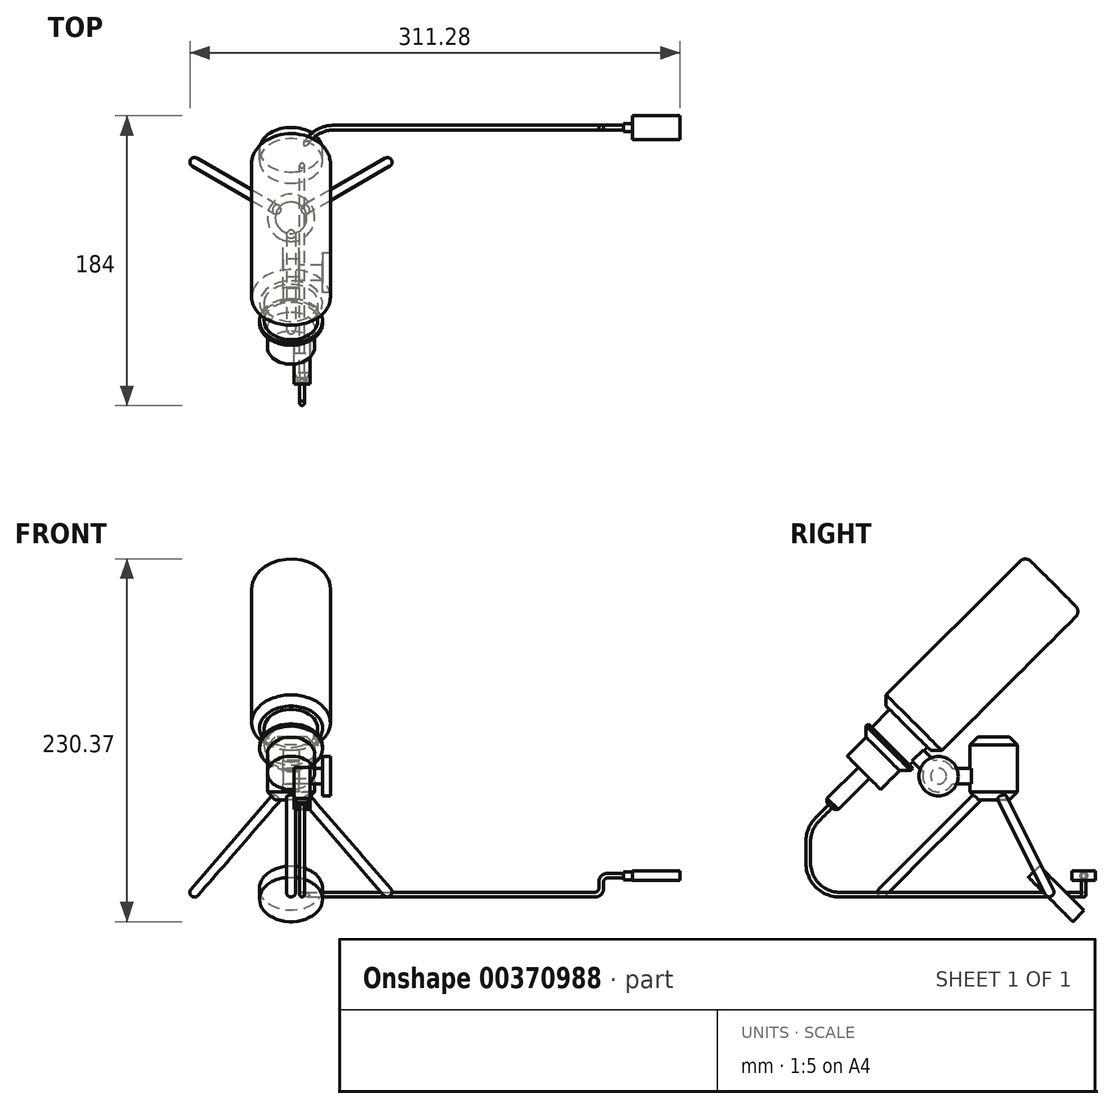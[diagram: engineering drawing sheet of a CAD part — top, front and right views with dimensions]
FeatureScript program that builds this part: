
annotation { "Feature Type Name" : "Feature", "Feature Type Description" : "" }
export const myFeature = defineFeature(function(context is Context, id is Id, definition is map)
    precondition{}
    {
        {
            var Q0;
            Q0=qCreatedBy(makeId("Top.planeOp"),FACE);
            var sketch = newSketch(context, id + "F0", { "sketchPlane" : qUnion([Q0])});
            skCircle(sketch, "E0", {"center": v(0, 0) * mm, "radius": 15 * mm});
            skSolve(sketch);
        }
        {
            var Q0;
            Q0 = qSketchRegion(id + "F0", true);
            extrude(context, id + "F1", {"entities" : qUnion([Q0]), "depth" : 40 * mm});
        }
        {
            var Q0;
            Q0=makeQuery(id+"F1.opExtrude","CAP_EDGE",EDGE,{"disambiguationData":[OSD([sQuery(id+"F0.wireOp",EDGE,"E0")])],"isStart":true});
            var Q1;
            Q1=makeQuery(id+"F1.opExtrude","CAP_EDGE",EDGE,{"disambiguationData":[OSD([sQuery(id+"F0.wireOp",EDGE,"E0")])],"isStart":false});
            chamfer(context, id + "F2", {"entities" : qUnion([Q0, Q1]), "width" : 5 * mm, "tangentPropagation" : true});
        }
        {
            var Q0;
            Q0=qCreatedBy(makeId("Right.planeOp"),FACE);
            var sketch = newSketch(context, id + "F3", { "sketchPlane" : qUnion([Q0])});
            skLineSegment(sketch, "E1", {"start": v(-72.83, -56.59) * mm, "end": v(-2.12, 14.12) * mm});
            skLineSegment(sketch, "E2", {"start": v(-2.12, 14.12) * mm, "end": v(0, 12) * mm});
            skArc(sketch, "E3", {"start": v(-72.83, -56.59) * mm, "mid": v(-73.71, -58.71) * mm, "end": v(-72.83, -60.83) * mm});
            skLineSegment(sketch, "E4", {"start": v(-72.83, -60.83) * mm, "end": v(0, 12) * mm});
            skSolve(sketch);
        }
        {
            var Q0;
            Q0 = qSketchRegion(id + "F3", true);
            var Q1;
            Q1=sQuery(id+"F3.wireOp",EDGE,"E4");
            revolve(context, id + "F4", {"operationType" : NewBodyOperationType.ADD, "entities" : qUnion([Q0]), "axis" : qUnion([Q1]), "revolveType" : RevolveType.FULL});
        }
        {
            var Q0;
            Q0=qCreatedBy(makeId("Right.planeOp"),FACE);
            var sketch = newSketch(context, id + "F5", { "sketchPlane" : qUnion([Q0])});
            skLineSegment(sketch, "E5", {"start": v(0, 0) * mm, "end": v(0, -28.47) * mm});
            skSolve(sketch);
        }
        {
            var Q0;
            Q0=qCreatedBy(makeId("Right.planeOp"),FACE);
            var Q1;
            Q1=sQuery(id+"F5.wireOp",EDGE,"E5");
            cPlane(context, id + "F6", {"entities" : qUnion([Q0, Q1]), "cplaneType" : CPlaneType.LINE_ANGLE, "offset" : 25 * mm, "angle" : 120 * degree, "oppositeDirection" : true, "width" : 150 * mm, "height" : 150 * mm});
        }
        {
            var Q0;
            Q0=qCreatedBy(id+"F6.planeOp",FACE);
            var sketch = newSketch(context, id + "F7", { "sketchPlane" : qUnion([Q0])});
            skLineSegment(sketch, "E6", {"start": v(0, 12) * mm, "end": v(72.73, -60.73) * mm});
            skLineSegment(sketch, "E7", {"start": v(72.73, -56.5) * mm, "end": v(2.02, 14.22) * mm});
            skLineSegment(sketch, "E8", {"start": v(2.02, 14.22) * mm, "end": v(0, 12) * mm});
            skArc(sketch, "E9", {"start": v(72.73, -56.5) * mm, "mid": v(73.61, -58.61) * mm, "end": v(72.73, -60.73) * mm});
            skPoint(sketch, "E10.orphan", {"position": v(70.61, -61.61) * mm});
            skSolve(sketch);
        }
        {
            var Q0;
            Q0 = qSketchRegion(id + "F7", true);
            var Q1;
            Q1=sQuery(id+"F7.wireOp",EDGE,"E6");
            revolve(context, id + "F8", {"operationType" : NewBodyOperationType.ADD, "entities" : qUnion([Q0]), "axis" : qUnion([Q1]), "revolveType" : RevolveType.FULL});
        }
        {
            var Q0;
            Q0=qCreatedBy(id+"F6.planeOp",FACE);
            var Q1;
            Q1=sQuery(id+"F5.wireOp",EDGE,"E5");
            cPlane(context, id + "F9", {"entities" : qUnion([Q0, Q1]), "cplaneType" : CPlaneType.LINE_ANGLE, "offset" : 25 * mm, "angle" : 120 * degree, "oppositeDirection" : true, "width" : 150 * mm, "height" : 150 * mm});
        }
        {
            var Q0;
            Q0=qCreatedBy(id+"F9.planeOp",FACE);
            var sketch = newSketch(context, id + "F10", { "sketchPlane" : qUnion([Q0])});
            skLineSegment(sketch, "E11", {"start": v(0, 12) * mm, "end": v(-72.89, -60.89) * mm});
            skLineSegment(sketch, "E12", {"start": v(-72.89, -56.64) * mm, "end": v(-2.18, 14.07) * mm});
            skLineSegment(sketch, "E13", {"start": v(-2.18, 14.07) * mm, "end": v(0, 12) * mm});
            skArc(sketch, "E14", {"start": v(-72.89, -56.64) * mm, "mid": v(-73.77, -58.77) * mm, "end": v(-72.89, -60.89) * mm});
            skPoint(sketch, "E15.orphan", {"position": v(-70.77, -61.77) * mm});
            skSolve(sketch);
        }
        {
            var Q0;
            Q0 = qSketchRegion(id + "F10", true);
            var Q1;
            Q1=sQuery(id+"F10.wireOp",EDGE,"E11");
            revolve(context, id + "F11", {"operationType" : NewBodyOperationType.ADD, "entities" : qUnion([Q0]), "axis" : qUnion([Q1]), "revolveType" : RevolveType.FULL});
        }
        {
            var Q0;
            Q0=qCreatedBy(makeId("Front.planeOp"),FACE);
            var sketch = newSketch(context, id + "F12", { "sketchPlane" : qUnion([Q0])});
            skLineSegment(sketch, "E16.bottom", {"start": v(-5, 20) * mm, "end": v(5, 20) * mm});
            skLineSegment(sketch, "E16.top", {"start": v(-5, 10) * mm, "end": v(5, 10) * mm});
            skLineSegment(sketch, "E16.left", {"start": v(-5, 20) * mm, "end": v(-5, 10) * mm});
            skLineSegment(sketch, "E16.right", {"start": v(5, 20) * mm, "end": v(5, 10) * mm});
            skSolve(sketch);
        }
        {
            var Q0;
            Q0 = qSketchRegion(id + "F12", true);
            extrude(context, id + "F13", {"entities" : qUnion([Q0]), "operationType" : NewBodyOperationType.ADD, "depth" : 30 * mm});
        }
        {
            var Q0;
            Q0=qCreatedBy(makeId("Right.planeOp"),FACE);
            var sketch = newSketch(context, id + "F14", { "sketchPlane" : qUnion([Q0])});
            skCircle(sketch, "E17", {"center": v(-35, 15) * mm, "radius": 10 * mm});
            skLineSegment(sketch, "E18", {"start": v(-38.54, 11.46) * mm, "end": v(-35, 15) * mm});
            skLineSegment(sketch, "E19", {"start": v(-38.54, 11.46) * mm, "end": v(-52.68, 25.6) * mm});
            skLineSegment(sketch, "E20", {"start": v(-52.68, 25.6) * mm, "end": v(-45.6, 32.68) * mm});
            skLineSegment(sketch, "E21", {"start": v(-45.6, 32.68) * mm, "end": v(-31.46, 18.54) * mm});
            skLineSegment(sketch, "E22", {"start": v(-31.46, 18.54) * mm, "end": v(-35, 15) * mm});
            skSolve(sketch);
        }
        {
            var Q0;
            Q0 = qSketchRegion(id + "F14", true);
            extrude(context, id + "F15", {"entities" : qUnion([Q0]), "operationType" : NewBodyOperationType.ADD, "endBound" : BoundingType.SYMMETRIC, "depth" : 10 * mm});
        }
        {
            var Q0;
            Q0=makeQuery(id+"F15.opExtrude","SWEPT_FACE",FACE,{"disambiguationData":[OSD([sQuery(id+"F14.wireOp",EDGE,"E21")])]});
            var sketch = newSketch(context, id + "F16", { "sketchPlane" : qUnion([Q0])});
            skPoint(sketch, "E23.first.point", {"position": v(0, -67.78) * mm});
            skPoint(sketch, "E23.first.point.positionSnap0", {"position": v(0, -55.36) * mm});
            skPoint(sketch, "E23.second.point", {"position": v(0, -49.63) * mm});
            skPoint(sketch, "E23.second.point.positionSnap0", {"position": v(0, -55.36) * mm});
            skPoint(sketch, "E23.third.point", {"position": v(-9.57, -55.36) * mm});
            skPoint(sketch, "E23.third.point.positionSnap0", {"position": v(0, -55.36) * mm});
            skCircle(sketch, "E24", {"center": v(0, -70.36) * mm, "radius": 20 * mm});
            skSolve(sketch);
        }
        {
            var Q0;
            Q0 = qSketchRegion(id + "F16", true);
            extrude(context, id + "F17", {"entities" : qUnion([Q0]), "operationType" : NewBodyOperationType.ADD, "oppositeDirection" : true, "depth" : 10 * mm});
        }
        {
            var Q0;
            Q0=qCreatedBy(makeId("Right.planeOp"),FACE);
            var sketch = newSketch(context, id + "F18", { "sketchPlane" : qUnion([Q0])});
            skLineSegment(sketch, "E25", {"start": v(-82.38, 17.12) * mm, "end": v(37.83, 137.33) * mm});
            skLineSegment(sketch, "E26", {"start": v(37.83, 137.33) * mm, "end": v(20.15, 155) * mm});
            skLineSegment(sketch, "E27", {"start": v(20.15, 155) * mm, "end": v(-71.77, 63.08) * mm});
            skLineSegment(sketch, "E28", {"start": v(-71.77, 63.08) * mm, "end": v(-66.11, 57.43) * mm});
            skLineSegment(sketch, "E29", {"start": v(-66.11, 57.43) * mm, "end": v(-77.43, 46.11) * mm});
            skLineSegment(sketch, "E30", {"start": v(-84.5, 43.28) * mm, "end": v(-80.96, 39.75) * mm});
            skLineSegment(sketch, "E31", {"start": v(-89.45, 24.2) * mm, "end": v(-82.38, 17.12) * mm});
            skPoint(sketch, "E32.end.orphan", {"position": v(-71.77, 45.43) * mm});
            skLineSegment(sketch, "E33", {"start": v(-77.43, 46.11) * mm, "end": v(-79.55, 48.23) * mm});
            skLineSegment(sketch, "E34", {"start": v(-79.55, 48.23) * mm, "end": v(-84.5, 43.28) * mm});
            skLineSegment(sketch, "E35", {"start": v(-80.96, 39.75) * mm, "end": v(-92.98, 27.73) * mm});
            skLineSegment(sketch, "E36", {"start": v(-92.98, 27.73) * mm, "end": v(-89.45, 24.2) * mm});
            skPoint(sketch, "E37.start.orphan", {"position": v(-77.43, 36.21) * mm});
            skSolve(sketch);
        }
        {
            var Q0;
            Q0 = qSketchRegion(id + "F18", true);
            var Q1;
            Q1=sQuery(id+"F18.wireOp",EDGE,"E25");
            revolve(context, id + "F19", {"operationType" : NewBodyOperationType.ADD, "entities" : qUnion([Q0]), "axis" : qUnion([Q1]), "revolveType" : RevolveType.FULL});
        }
        {
            var Q0;
            Q0=makeQuery(id+"F19.opRevolve","SWEPT_EDGE",EDGE,{"disambiguationData":[OSD([sQuery(id+"F18.wireOp",EDGE,"E26"),sQuery(id+"F18.wireOp",EDGE,"E27")])]});
            fillet(context, id + "F20", {"entities" : qUnion([Q0]), "radius" : 5 * mm, "tangentPropagation" : true, "allowEdgeOverflow" : false});
        }
        {
            var Q0;
            Q0=makeQuery(id+"F19.opRevolve","SWEPT_EDGE",EDGE,{"disambiguationData":[OSD([sQuery(id+"F18.wireOp",EDGE,"E27"),sQuery(id+"F18.wireOp",EDGE,"E28")])]});
            var Q1;
            Q1=makeQuery(id+"F19.opRevolve","SWEPT_EDGE",EDGE,{"disambiguationData":[OSD([sQuery(id+"F18.wireOp",EDGE,"E30"),sQuery(id+"F18.wireOp",EDGE,"E34")])]});
            chamfer(context, id + "F21", {"entities" : qUnion([Q0, Q1]), "width" : 5 * mm, "tangentPropagation" : true});
        }
        {
            var Q0;
            Q0=makeQuery(id+"F15.boolean.opBoolean","MERGE",FACE,{"derivedFrom":[makeQuery(id+"F13.opExtrude","SWEPT_FACE",FACE,{"disambiguationData":[OSD([sQuery(id+"F12.wireOp",EDGE,"E16.right")])]}),makeQuery(id+"F15.opExtrude","CAP_FACE",FACE,{"disambiguationData":[OSD([sQuery(id+"F14.wireOp",EDGE,"E17"),sQuery(id+"F14.wireOp",EDGE,"E19"),sQuery(id+"F14.wireOp",EDGE,"E20"),sQuery(id+"F14.wireOp",EDGE,"E21")])],"isStart":false})]});
            var sketch = newSketch(context, id + "F22", { "sketchPlane" : qUnion([Q0])});
            skCircle(sketch, "E38", {"center": v(-35, 15) * mm, "radius": 5 * mm});
            skSolve(sketch);
        }
        {
            var Q0;
            Q0 = qSketchRegion(id + "F22", true);
            extrude(context, id + "F23", {"entities" : qUnion([Q0]), "operationType" : NewBodyOperationType.ADD, "depth" : 15 * mm});
        }
        {
            var Q0;
            Q0=makeQuery(id+"F23.opExtrude","CAP_FACE",FACE,{"disambiguationData":[OSD([sQuery(id+"F22.wireOp",EDGE,"E38")])],"isStart":false});
            var sketch = newSketch(context, id + "F24", { "sketchPlane" : qUnion([Q0])});
            skCircle(sketch, "E39", {"center": v(-35, 15) * mm, "radius": 12.5 * mm});
            skSolve(sketch);
        }
        {
            var Q0;
            Q0 = qSketchRegion(id + "F24", true);
            extrude(context, id + "F25", {"entities" : qUnion([Q0]), "operationType" : NewBodyOperationType.ADD, "depth" : 5 * mm});
        }
        {
            var Q0;
            Q0=makeQuery(id+"F19.opRevolve","SWEPT_FACE",FACE,{"disambiguationData":[OSD([sQuery(id+"F18.wireOp",EDGE,"E31")])]});
            var sketch = newSketch(context, id + "F26", { "sketchPlane" : qUnion([Q0])});
            skLineSegment(sketch, "E40.bottom", {"start": v(2, 65.36) * mm, "end": v(12, 65.36) * mm});
            skLineSegment(sketch, "E40.top", {"start": v(2, 75.36) * mm, "end": v(12, 75.36) * mm});
            skLineSegment(sketch, "E40.left", {"start": v(2, 65.36) * mm, "end": v(2, 75.36) * mm});
            skLineSegment(sketch, "E40.right", {"start": v(12, 65.36) * mm, "end": v(12, 75.36) * mm});
            skSolve(sketch);
        }
        {
            var Q0;
            Q0 = qSketchRegion(id + "F26", true);
            extrude(context, id + "F27", {"entities" : qUnion([Q0]), "operationType" : NewBodyOperationType.ADD, "depth" : 30 * mm});
        }
        {
            var Q0;
            Q0=makeQuery(id+"F27.opExtrude","CAP_FACE",FACE,{"disambiguationData":[OSD([sQuery(id+"F26.wireOp",EDGE,"E40.bottom"),sQuery(id+"F26.wireOp",EDGE,"E40.top"),sQuery(id+"F26.wireOp",EDGE,"E40.left"),sQuery(id+"F26.wireOp",EDGE,"E40.right")])],"isStart":false});
            chamfer(context, id + "F28", {"entities" : qUnion([Q0]), "width" : 2 * mm, "tangentPropagation" : true});
        }
        {
            var Q0;
            Q0=qCreatedBy(makeId("Right.planeOp"),FACE);
            var sketch = newSketch(context, id + "F29", { "sketchPlane" : qUnion([Q0])});
            skLineSegment(sketch, "E41", {"start": v(-103.59, -4.1) * mm, "end": v(-111.87, -12.38) * mm});
            skLineSegment(sketch, "E42", {"start": v(-117.73, -26.52) * mm, "end": v(-117.73, -40.23) * mm});
            skLineSegment(sketch, "E43", {"start": v(-97.73, -60.23) * mm, "end": v(32.27, -60.23) * mm});
            skPoint(sketch, "E44.visualSharp", {"position": v(-117.73, -18.23) * mm});
            skArc(sketch, "E44.filletArc", {"start": v(-111.87, -12.38) * mm, "mid": v(-116.2, -18.86) * mm, "end": v(-117.73, -26.52) * mm});
            skPoint(sketch, "E45.visualSharp", {"position": v(-117.73, -60.23) * mm});
            skArc(sketch, "E45.filletArc", {"start": v(-117.73, -40.23) * mm, "mid": v(-111.87, -54.38) * mm, "end": v(-97.73, -60.23) * mm});
            skSolve(sketch);
        }
        {
            var Q0;
            Q0=makeQuery(id+"F27.opExtrude","CAP_FACE",FACE,{"disambiguationData":[OSD([sQuery(id+"F26.wireOp",EDGE,"E40.bottom"),sQuery(id+"F26.wireOp",EDGE,"E40.top"),sQuery(id+"F26.wireOp",EDGE,"E40.left"),sQuery(id+"F26.wireOp",EDGE,"E40.right")])],"isStart":false});
            var sketch = newSketch(context, id + "F30", { "sketchPlane" : qUnion([Q0])});
            skCircle(sketch, "E46", {"center": v(7, 70.36) * mm, "radius": 1.5 * mm});
            skSolve(sketch);
        }
        {
            var Q0;
            Q0 = qSketchRegion(id + "F30", true);
            var Q1;
            Q1 = qConstructionFilter(qBodyType(qCreatedBy(id + "F29" ,EDGE), BodyType.WIRE), ConstructionObject.NO);
            sweep(context, id + "F31", {"operationType" : NewBodyOperationType.ADD, "profiles" : qUnion([Q0]), "path" : qUnion([Q1])});
        }
        {
            var Q0;
            Q0=makeQuery(id+"F31.opSweep","CAP_FACE",FACE,{"disambiguationData":[OSD([sQuery(id+"F29.wireOp",VERTEX,"E43.end"),sQuery(id+"F30.wireOp",EDGE,"E46")])],"isStart":false});
            var sketch = newSketch(context, id + "F32", { "sketchPlane" : qUnion([Q0])});
            skCircle(sketch, "E47", {"center": v(-7, -60.23) * mm, "radius": 1.5 * mm});
            skSolve(sketch);
        }
        {
            var Q0;
            Q0 = qBodyType(qCreatedBy(id + "F32" ,EDGE), BodyType.WIRE);
            cPlane(context, id + "F33", {"entities" : qUnion([Q0]), "cplaneType" : CPlaneType.LINE_ANGLE, "offset" : 25 * mm, "angle" : 0 * degree, "width" : 150 * mm, "height" : 150 * mm});
        }
        {
            var Q0;
            Q0=qCreatedBy(id+"F33.planeOp",FACE);
            var sketch = newSketch(context, id + "F34", { "sketchPlane" : qUnion([Q0])});
            skLineSegment(sketch, "E48", {"start": v(27, 57.27) * mm, "end": v(177, 57.27) * mm});
            skLineSegment(sketch, "E49", {"start": v(7, 32.27) * mm, "end": v(7, 37.27) * mm});
            skArc(sketch, "E50", {"start": v(7, 37.27) * mm, "mid": v(12.86, 51.41) * mm, "end": v(27, 57.27) * mm});
            skSolve(sketch);
        }
        {
            var Q0;
            Q0 = qSketchRegion(id + "F32", true);
            var Q1;
            Q1 = qConstructionFilter(qBodyType(qCreatedBy(id + "F34" ,EDGE), BodyType.WIRE), ConstructionObject.NO);
            sweep(context, id + "F35", {"operationType" : NewBodyOperationType.ADD, "profiles" : qUnion([Q0]), "path" : qUnion([Q1])});
        }
        {
            var Q0;
            Q0=makeQuery(id+"F35.opSweep","CAP_FACE",FACE,{"disambiguationData":[OSD([sQuery(id+"F32.wireOp",EDGE,"E47"),sQuery(id+"F34.wireOp",VERTEX,"E48.end")])],"isStart":false});
            var sketch = newSketch(context, id + "F36", { "sketchPlane" : qUnion([Q0])});
            skCircle(sketch, "E51", {"center": v(57.27, -60.23) * mm, "radius": 1.5 * mm});
            skSolve(sketch);
        }
        {
            var Q0;
            Q0=sQuery(id+"F36.wireOp",EDGE,"E51");
            cPlane(context, id + "F37", {"entities" : qUnion([Q0]), "cplaneType" : CPlaneType.LINE_ANGLE, "offset" : 25 * mm, "angle" : 0 * degree, "width" : 150 * mm, "height" : 150 * mm});
        }
        {
            var Q0;
            Q0=qCreatedBy(id+"F37.planeOp",FACE);
            var sketch = newSketch(context, id + "F38", { "sketchPlane" : qUnion([Q0])});
            skLineSegment(sketch, "E52", {"start": v(-177, -60.23) * mm, "end": v(-193, -60.23) * mm});
            skLineSegment(sketch, "E53", {"start": v(-197, -56.23) * mm, "end": v(-197, -52.23) * mm});
            skLineSegment(sketch, "E54", {"start": v(-201, -48.23) * mm, "end": v(-217, -48.23) * mm});
            skArc(sketch, "E55", {"start": v(-193, -60.23) * mm, "mid": v(-195.83, -59.06) * mm, "end": v(-197, -56.23) * mm});
            skArc(sketch, "E56", {"start": v(-197, -52.23) * mm, "mid": v(-198.17, -49.4) * mm, "end": v(-201, -48.23) * mm});
            skPoint(sketch, "E57.0", {"position": v(-177, -60.23) * mm});
            skSolve(sketch);
        }
        {
            var Q0;
            Q0 = qSketchRegion(id + "F36", true);
            var Q1;
            Q1 = qConstructionFilter(qBodyType(qCreatedBy(id + "F38" ,EDGE), BodyType.WIRE), ConstructionObject.NO);
            sweep(context, id + "F39", {"operationType" : NewBodyOperationType.ADD, "profiles" : qUnion([Q0]), "path" : qUnion([Q1])});
        }
        {
            var Q0;
            Q0=makeQuery(id+"F39.opSweep","CAP_FACE",FACE,{"disambiguationData":[OSD([sQuery(id+"F36.wireOp",EDGE,"E51"),sQuery(id+"F38.wireOp",VERTEX,"E54.end")])],"isStart":false});
            var sketch = newSketch(context, id + "F40", { "sketchPlane" : qUnion([Q0])});
            skLineSegment(sketch, "E58.bottom", {"start": v(49.77, -51.23) * mm, "end": v(64.77, -51.23) * mm});
            skLineSegment(sketch, "E58.top", {"start": v(49.77, -45.23) * mm, "end": v(64.77, -45.23) * mm});
            skLineSegment(sketch, "E58.left", {"start": v(49.77, -51.23) * mm, "end": v(49.77, -45.23) * mm});
            skLineSegment(sketch, "E58.right", {"start": v(64.77, -51.23) * mm, "end": v(64.77, -45.23) * mm});
            skPoint(sketch, "E58.middle", {"position": v(57.27, -48.23) * mm});
            skSolve(sketch);
        }
        {
            var Q0;
            Q0 = qSketchRegion(id + "F40", true);
            extrude(context, id + "F41", {"entities" : qUnion([Q0]), "operationType" : NewBodyOperationType.ADD, "depth" : 30 * mm});
        }
        {
            var Q0;
            Q0=makeQuery(id+"F41.opExtrude","CAP_FACE",FACE,{"disambiguationData":[OSD([sQuery(id+"F40.wireOp",EDGE,"E58.bottom"),sQuery(id+"F40.wireOp",EDGE,"E58.top"),sQuery(id+"F40.wireOp",EDGE,"E58.left"),sQuery(id+"F40.wireOp",EDGE,"E58.right")])],"isStart":true});
            var sketch = newSketch(context, id + "F42", { "sketchPlane" : qUnion([Q0])});
            skCircle(sketch, "E59", {"center": v(-57.27, -48.23) * mm, "radius": 2.5 * mm});
            skSolve(sketch);
        }
        {
            var Q0;
            Q0 = qSketchRegion(id + "F42", true);
            extrude(context, id + "F43", {"entities" : qUnion([Q0]), "operationType" : NewBodyOperationType.ADD, "depth" : 6 * mm});
        }
    });
